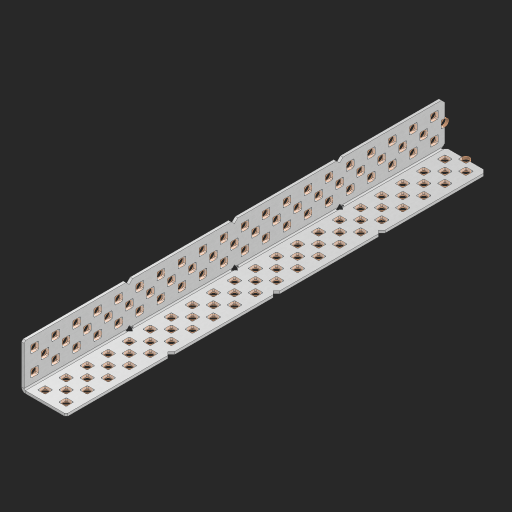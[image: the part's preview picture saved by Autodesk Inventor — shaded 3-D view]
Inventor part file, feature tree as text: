
AUTODESK INVENTOR PART (.ipt)
format: ipt  version: 2023 (Build 270158000, 158)  size: 1,504,768 bytes
history: native  units: in
note: dims shown in document units (in); Inventor stores cm internally (conversion verified against a paired STEP export)
features: other x126, extrude x118, sheet_metal_op x8, sketch x7, pattern_linear x2, mirror x1, chamfer x1
ambient origin geometry x8: Origin, YZ Plane, XZ Plane, XY Plane, X Axis, Y Axis, Z Axis, Center Point
bodies: Solid1 (feature_tree), Body (feature_tree)
feature tree (263):
  sheet_metal_op  "Flanges"
  sheet_metal_op  "Body Pattern"
  pattern_linear  "Center Pattern"  Spacing1=1.0in  [1 undecoded]
  other  "Arc Length"
  pattern_linear  "Notch Pattern"  Spacing1=0.25in  [1 undecoded]
  other  "Diagonal Plane"
  mirror  "Everything Mirrored"
  chamfer  "End Chamfer"
  sketch  "Sketch1"  dims[d0=1.0in]
  other  "Plate1"
  sketch  "Sketch2"  dims[d1=10.0in]
  other  "Plate2"
  sheet_metal_op  "Bend1"
  sheet_metal_op  "Corner1"
  sketch  "Sketch8"  dims[d2=0.0625in]
  sketch  "Sketch9"  dims[d3=0.0625in]
  other  "Srf91"
  sheet_metal_op  "Body Pattern Sketch"
  other  "Srf92"
  sketch  "Sketch13"  dims[d4=0.0312in]
  sketch  "Sketch15"  dims[d5=0.125in]
  sketch  "Sketch16"  dims[d6=0.0625in d7=1.0in d8=90.0deg d9=0.0312in d10=0.25in d11=0.0625in d12=0.0625in d49=0.182in d50=0.02in d52=0.25in d53=0.0625in d54=0.0in d55=0.172in d56=1.0in d57=0.0in d60=7.874in d62=0.5in d63=0.7874in d65=0.5in d85=0.1473in d86=0.1782in d89=0.0625in d90=0.0in d91=0.04in d92=0.0491in d95=2.5in d96=0.04in d97=0.25in d98=45.0deg d99=0.25in d106=0.182in d107=0.02in d108=0.5in d110=0.0625in d111=0.0in d112=0.172in d113=0.5in d114=0.0in d117=0.5in d123=0.25in d125=0.25in d126=0.0491in d127=0.1473in d128=0.08in d129=0.04in d130=2.5in]
  other  "Srf786"
  other  "Srf856"
  other  "Srf857"
  other  "Srf858"
  other  "Srf859"
  other  "Srf860"
  other  "Srf861"
  other  "Srf889"
  other  "Srf890"
  other  "Srf891"
  other  "Srf1275"
  other  "Srf1276"
  other  "Srf1278"
  other  "Srf1279"
  other  "Srf1280"
  other  "Srf1281"
  other  "Srf1282"
  other  "Srf1283"
  other  "Srf1277"
  other  "Srf1285"
  other  "Srf1286"
  other  "Srf1287"
  other  "Srf1383"
  other  "Srf1384"
  other  "Srf1385"
  other  "Srf1386"
  other  "Srf1387"
  other  "Srf1388"
  other  "Srf1389"
  other  "Srf1390"
  other  "Srf1391"
  other  "Srf1392"
  other  "Srf1393"
  other  "Srf1394"
  other  "Srf1395"
  other  "Srf1396"
  other  "Srf1397"
  other  "Srf1398"
  other  "Srf1399"
  other  "Srf1400"
  other  "Srf1401"
  other  "Srf1402"
  other  "Srf1403"
  other  "Srf1404"
  other  "Srf1405"
  other  "Srf1406"
  other  "Srf1407"
  other  "Srf1408"
  other  "Srf1409"
  other  "Srf1410"
  other  "Srf1411"
  other  "Srf1412"
  other  "Srf1413"
  other  "Srf1414"
  other  "Srf1445"
  other  "Srf1446"
  other  "Srf1447"
  other  "Srf1448"
  other  "Srf1449"
  other  "Srf1450"
  other  "Srf1451"
  other  "Srf1452"
  other  "Srf1453"
  other  "Srf1454"
  other  "Srf1455"
  other  "Srf1456"
  other  "Srf1457"
  other  "Srf1458"
  other  "Srf1459"
  other  "Srf1460"
  other  "Srf1475"
  other  "Srf1476"
  other  "Srf1477"
  other  "Srf1478"
  other  "Srf1479"
  other  "Srf1480"
  other  "Srf1481"
  other  "Srf1482"
  other  "Srf1483"
  other  "Srf1484"
  other  "Srf1485"
  other  "Srf1486"
  other  "Srf1487"
  other  "Srf1488"
  other  "Srf1489"
  other  "Srf1490"
  other  "Srf1491"
  other  "Srf1492"
  other  "Srf1493"
  other  "Srf1494"
  other  "Srf1495"
  other  "Srf1496"
  other  "Srf1497"
  other  "Srf1498"
  other  "Srf1499"
  other  "Srf1500"
  other  "Srf1501"
  other  "Srf1502"
  other  "Srf1503"
  other  "Srf1504"
  other  "Srf1505"
  other  "Srf1506"
  other  "Srf1537"
  other  "Srf1538"
  other  "Srf1539"
  other  "Srf1540"
  other  "Srf1541"
  other  "Srf1542"
  other  "Srf1543"
  other  "Srf1544"
  other  "Srf1545"
  other  "Srf1546"
  other  "Srf1547"
  other  "Srf1548"
  other  "Srf1549"
  other  "Srf1550"
  other  "Srf1551"
  other  "Srf1552"
  sheet_metal_op  "Body Stamp"
  sheet_metal_op  "Body Circle"
  other  "Center Stamp"
  other  "Center Circle"
  sheet_metal_op  "Notch"
  extrude  "ExtrusionSrf92"  Depth=0.0625in
  extrude  "ExtrusionSrf856"  Depth=0.0625in
  extrude  "ExtrusionSrf857"  Depth=2.5in
  extrude  "ExtrusionSrf858"  Depth=0.02in
  extrude  "ExtrusionSrf859"  Depth=2.5in
  extrude  "ExtrusionSrf860"  Depth=0.0625in
  extrude  "ExtrusionSrf861"  TaperAngle=0.0deg  [1 undecoded]
  extrude  "ExtrusionSrf889"  Depth=2.5in
  extrude  "ExtrusionSrf890"  Depth=1.0in TaperAngle=0.0deg
  extrude  "ExtrusionSrf891"  Depth=2.5in
  extrude  "ExtrusionSrf1275"  Depth=0.5in
  extrude  "ExtrusionSrf1276"  Depth=2.5in
  extrude  "ExtrusionSrf1277"  Depth=2.5in
  extrude  "ExtrusionSrf1278"  Depth=0.0625in
  extrude  "ExtrusionSrf1279"  Depth=2.5in TaperAngle=0.0deg
  extrude  "ExtrusionSrf1280"  Depth=2.5in
  extrude  "ExtrusionSrf1281"  Depth=2.5in TaperAngle=45.0deg
  extrude  "ExtrusionSrf1282"  Depth=2.5in
  extrude  "ExtrusionSrf1345"  Depth=2.5in
  extrude  "ExtrusionSrf1346"  Depth=0.02in
  extrude  "ExtrusionSrf1347"  Depth=0.5in
  extrude  "ExtrusionSrf1348"  Depth=0.0625in
  extrude  "ExtrusionSrf1383"  TaperAngle=0.0deg  [1 undecoded]
  extrude  "ExtrusionSrf1384"  Depth=2.5in
  extrude  "ExtrusionSrf1385"  Depth=0.5in TaperAngle=0.0deg
  extrude  "ExtrusionSrf1386"  Depth=0.5in
  extrude  "ExtrusionSrf1387"  Depth=2.5in
  extrude  "ExtrusionSrf1388"  Depth=2.5in
  extrude  "ExtrusionSrf1389"  Depth=2.5in
  extrude  "ExtrusionSrf1390"  Depth=2.5in
  extrude  "ExtrusionSrf1391"  Depth=2.5in
  extrude  "ExtrusionSrf1392"  Depth=2.5in
  extrude  "ExtrusionSrf1393"  Depth=2.5in
  extrude  "ExtrusionSrf1394"  [1 undecoded]
  extrude  "ExtrusionSrf1395"  [1 undecoded]
  extrude  "ExtrusionSrf1396"  [1 undecoded]
  extrude  "ExtrusionSrf1397"  [1 undecoded]
  extrude  "ExtrusionSrf1398"  [1 undecoded]
  extrude  "ExtrusionSrf1399"  [1 undecoded]
  extrude  "ExtrusionSrf1400"  [1 undecoded]
  extrude  "ExtrusionSrf1401"  [1 undecoded]
  extrude  "ExtrusionSrf1402"  [1 undecoded]
  extrude  "ExtrusionSrf1403"  [1 undecoded]
  extrude  "ExtrusionSrf1404"  [1 undecoded]
  extrude  "ExtrusionSrf1405"  [1 undecoded]
  extrude  "ExtrusionSrf1406"  [1 undecoded]
  extrude  "ExtrusionSrf1407"  [1 undecoded]
  extrude  "ExtrusionSrf1408"  [1 undecoded]
  extrude  "ExtrusionSrf1409"  [1 undecoded]
  extrude  "ExtrusionSrf1410"  [1 undecoded]
  extrude  "ExtrusionSrf1411"  [1 undecoded]
  extrude  "ExtrusionSrf1412"  [1 undecoded]
  extrude  "ExtrusionSrf1413"  [1 undecoded]
  extrude  "ExtrusionSrf1414"  [1 undecoded]
  extrude  "ExtrusionSrf1445"  [1 undecoded]
  extrude  "ExtrusionSrf1446"  [1 undecoded]
  extrude  "ExtrusionSrf1447"  [1 undecoded]
  extrude  "ExtrusionSrf1448"  [1 undecoded]
  extrude  "ExtrusionSrf1449"  [1 undecoded]
  extrude  "ExtrusionSrf1450"  [1 undecoded]
  extrude  "ExtrusionSrf1451"  [1 undecoded]
  extrude  "ExtrusionSrf1452"  [1 undecoded]
  extrude  "ExtrusionSrf1453"  [1 undecoded]
  extrude  "ExtrusionSrf1454"  [1 undecoded]
  extrude  "ExtrusionSrf1455"  [1 undecoded]
  extrude  "ExtrusionSrf1456"  [1 undecoded]
  extrude  "ExtrusionSrf1457"  [1 undecoded]
  extrude  "ExtrusionSrf1458"  [1 undecoded]
  extrude  "ExtrusionSrf1459"  [1 undecoded]
  extrude  "ExtrusionSrf1460"  [1 undecoded]
  extrude  "ExtrusionSrf1475"  [1 undecoded]
  extrude  "ExtrusionSrf1476"  [1 undecoded]
  extrude  "ExtrusionSrf1477"  [1 undecoded]
  extrude  "ExtrusionSrf1478"  [1 undecoded]
  extrude  "ExtrusionSrf1479"  [1 undecoded]
  extrude  "ExtrusionSrf1480"  [1 undecoded]
  extrude  "ExtrusionSrf1481"  [1 undecoded]
  extrude  "ExtrusionSrf1482"  [1 undecoded]
  extrude  "ExtrusionSrf1483"  [1 undecoded]
  extrude  "ExtrusionSrf1484"  [1 undecoded]
  extrude  "ExtrusionSrf1485"  [1 undecoded]
  extrude  "ExtrusionSrf1486"  [1 undecoded]
  extrude  "ExtrusionSrf1487"  [1 undecoded]
  extrude  "ExtrusionSrf1488"  [1 undecoded]
  extrude  "ExtrusionSrf1489"  [1 undecoded]
  extrude  "ExtrusionSrf1490"  [1 undecoded]
  extrude  "ExtrusionSrf1491"  [1 undecoded]
  extrude  "ExtrusionSrf1492"  [1 undecoded]
  extrude  "ExtrusionSrf1493"  [1 undecoded]
  extrude  "ExtrusionSrf1494"  [1 undecoded]
  extrude  "ExtrusionSrf1495"  [1 undecoded]
  extrude  "ExtrusionSrf1496"  [1 undecoded]
  extrude  "ExtrusionSrf1497"  [1 undecoded]
  extrude  "ExtrusionSrf1498"  [1 undecoded]
  extrude  "ExtrusionSrf1499"  [1 undecoded]
  extrude  "ExtrusionSrf1500"  [1 undecoded]
  extrude  "ExtrusionSrf1501"  [1 undecoded]
  extrude  "ExtrusionSrf1502"  [1 undecoded]
  extrude  "ExtrusionSrf1503"  [1 undecoded]
  extrude  "ExtrusionSrf1504"  [1 undecoded]
  extrude  "ExtrusionSrf1505"  [1 undecoded]
  extrude  "ExtrusionSrf1506"  [1 undecoded]
  extrude  "ExtrusionSrf1537"  [1 undecoded]
  extrude  "ExtrusionSrf1538"  [1 undecoded]
  extrude  "ExtrusionSrf1539"  [1 undecoded]
  extrude  "ExtrusionSrf1540"  [1 undecoded]
  extrude  "ExtrusionSrf1541"  [1 undecoded]
  extrude  "ExtrusionSrf1542"  [1 undecoded]
  extrude  "ExtrusionSrf1543"  [1 undecoded]
  extrude  "ExtrusionSrf1544"  [1 undecoded]
  extrude  "ExtrusionSrf1545"  [1 undecoded]
  extrude  "ExtrusionSrf1546"  [1 undecoded]
  extrude  "ExtrusionSrf1547"  [1 undecoded]
  extrude  "ExtrusionSrf1548"  [1 undecoded]
  extrude  "ExtrusionSrf1549"  [1 undecoded]
  extrude  "ExtrusionSrf1550"  [1 undecoded]
  extrude  "ExtrusionSrf1551"  [1 undecoded]
  extrude  "ExtrusionSrf1552"  [1 undecoded]
note: 89 required parameter values undecoded (feature->parameter linkage not recoverable at this tier; creation-order binding heuristic only, values carry confidence <= 0.55)
